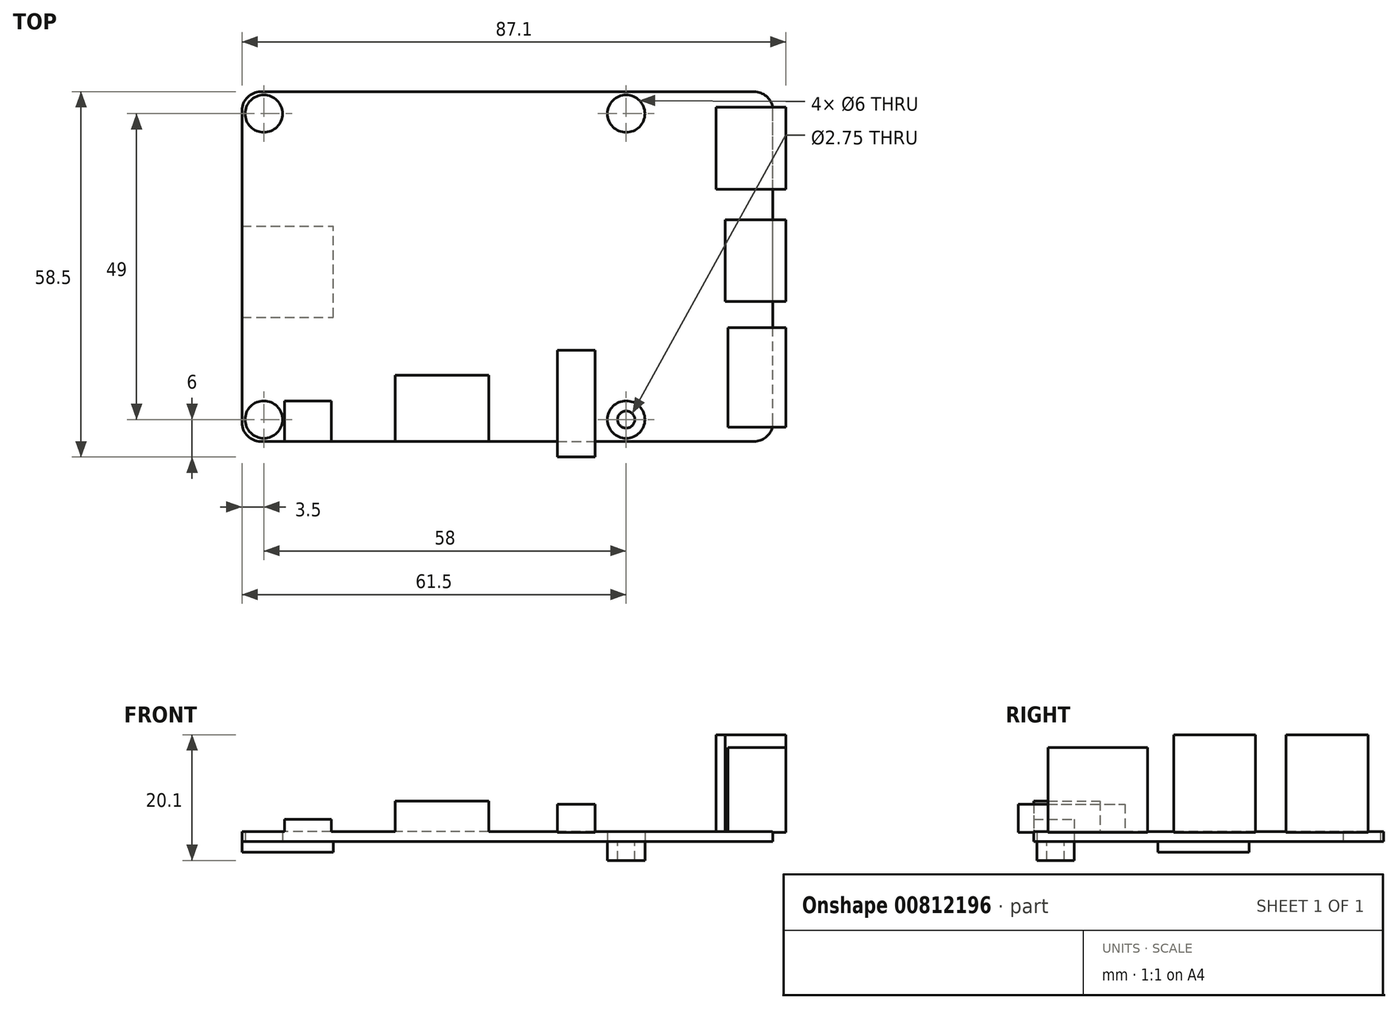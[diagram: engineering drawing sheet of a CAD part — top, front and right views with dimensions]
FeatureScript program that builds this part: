
annotation { "Feature Type Name" : "Feature", "Feature Type Description" : "" }
export const myFeature = defineFeature(function(context is Context, id is Id, definition is map)
    precondition{}
    {
        {
            var Q0;
            Q0=qCreatedBy(makeId("Top.planeOp"),FACE);
            var sketch = newSketch(context, id + "F0", { "sketchPlane" : qUnion([Q0])});
            skLineSegment(sketch, "E0.bottom", {"start": v(-39.5, -28) * mm, "end": v(39.5, -28) * mm});
            skLineSegment(sketch, "E0.top", {"start": v(-39.5, 28) * mm, "end": v(39.5, 28) * mm});
            skLineSegment(sketch, "E0.left", {"start": v(-42.5, -25) * mm, "end": v(-42.5, 25) * mm});
            skLineSegment(sketch, "E0.right", {"start": v(42.5, -25) * mm, "end": v(42.5, 25) * mm});
            skPoint(sketch, "E0.middle", {"position": v(0, 0) * mm});
            skLineSegment(sketch, "E1.bottom", {"start": v(-39, 24.5) * mm, "end": v(19, 24.5) * mm, "construction": true});
            skLineSegment(sketch, "E1.top", {"start": v(-39, -24.5) * mm, "end": v(19, -24.5) * mm, "construction": true});
            skLineSegment(sketch, "E1.left", {"start": v(-39, 24.5) * mm, "end": v(-39, -24.5) * mm, "construction": true});
            skLineSegment(sketch, "E1.right", {"start": v(19, 24.5) * mm, "end": v(19, -24.5) * mm, "construction": true});
            skCircle(sketch, "E2", {"center": v(-39, 24.5) * mm, "radius": 1.38 * mm});
            skPoint(sketch, "E3.visualSharp", {"position": v(-42.5, 28) * mm});
            skArc(sketch, "E3.filletArc", {"start": v(-39.5, 28) * mm, "mid": v(-41.62, 27.12) * mm, "end": v(-42.5, 25) * mm});
            skPoint(sketch, "E4.visualSharp", {"position": v(42.5, 28) * mm});
            skArc(sketch, "E4.filletArc", {"start": v(42.5, 25) * mm, "mid": v(41.62, 27.12) * mm, "end": v(39.5, 28) * mm});
            skPoint(sketch, "E5.visualSharp", {"position": v(-42.5, -28) * mm});
            skArc(sketch, "E5.filletArc", {"start": v(-42.5, -25) * mm, "mid": v(-41.62, -27.12) * mm, "end": v(-39.5, -28) * mm});
            skPoint(sketch, "E6.visualSharp", {"position": v(42.5, -28) * mm});
            skArc(sketch, "E6.filletArc", {"start": v(39.5, -28) * mm, "mid": v(41.62, -27.12) * mm, "end": v(42.5, -25) * mm});
            skCircle(sketch, "E7", {"center": v(19, 24.5) * mm, "radius": 1.38 * mm});
            skCircle(sketch, "E8", {"center": v(19, -24.5) * mm, "radius": 1.38 * mm});
            skCircle(sketch, "E9", {"center": v(-39, -24.5) * mm, "radius": 1.38 * mm});
            skLineSegment(sketch, "E10.bottom", {"start": v(44.6, -25.7) * mm, "end": v(35.29, -25.7) * mm});
            skLineSegment(sketch, "E10.top", {"start": v(44.6, -9.8) * mm, "end": v(35.29, -9.8) * mm});
            skLineSegment(sketch, "E10.left", {"start": v(44.6, -25.7) * mm, "end": v(44.6, -9.8) * mm});
            skLineSegment(sketch, "E10.right", {"start": v(35.29, -25.7) * mm, "end": v(35.29, -9.8) * mm});
            skLineSegment(sketch, "E11.bottom", {"start": v(44.6, -5.6) * mm, "end": v(34.86, -5.6) * mm});
            skLineSegment(sketch, "E11.top", {"start": v(44.6, 7.5) * mm, "end": v(34.86, 7.5) * mm});
            skLineSegment(sketch, "E11.left", {"start": v(44.6, -5.6) * mm, "end": v(44.6, 7.5) * mm});
            skLineSegment(sketch, "E11.right", {"start": v(34.86, -5.6) * mm, "end": v(34.86, 7.5) * mm});
            skLineSegment(sketch, "E12.bottom", {"start": v(44.6, 12.4) * mm, "end": v(33.41, 12.4) * mm});
            skLineSegment(sketch, "E12.top", {"start": v(44.6, 25.5) * mm, "end": v(33.41, 25.5) * mm});
            skLineSegment(sketch, "E12.left", {"start": v(44.6, 12.4) * mm, "end": v(44.6, 25.5) * mm});
            skLineSegment(sketch, "E12.right", {"start": v(33.41, 12.4) * mm, "end": v(33.41, 25.5) * mm});
            skLineSegment(sketch, "E13.bottom", {"start": v(-42.5, -8.1) * mm, "end": v(-27.9, -8.1) * mm});
            skLineSegment(sketch, "E13.top", {"start": v(-42.5, 6.5) * mm, "end": v(-27.9, 6.5) * mm});
            skLineSegment(sketch, "E13.left", {"start": v(-42.5, -8.1) * mm, "end": v(-42.5, 6.5) * mm});
            skLineSegment(sketch, "E13.right", {"start": v(-27.9, -8.1) * mm, "end": v(-27.9, 6.5) * mm});
            skLineSegment(sketch, "E14.bottom", {"start": v(-35.7, -28) * mm, "end": v(-28.2, -28) * mm});
            skLineSegment(sketch, "E14.top", {"start": v(-35.7, -21.5) * mm, "end": v(-28.2, -21.5) * mm});
            skLineSegment(sketch, "E14.left", {"start": v(-35.7, -28) * mm, "end": v(-35.7, -21.5) * mm});
            skLineSegment(sketch, "E14.right", {"start": v(-28.2, -28) * mm, "end": v(-28.2, -21.5) * mm});
            skLineSegment(sketch, "E15.bottom", {"start": v(-18, -28) * mm, "end": v(-3, -28) * mm});
            skLineSegment(sketch, "E15.top", {"start": v(-18, -17.42) * mm, "end": v(-3, -17.42) * mm});
            skLineSegment(sketch, "E15.left", {"start": v(-18, -28) * mm, "end": v(-18, -17.42) * mm});
            skLineSegment(sketch, "E15.right", {"start": v(-3, -28) * mm, "end": v(-3, -17.42) * mm});
            skLineSegment(sketch, "E16.bottom", {"start": v(8, -30.5) * mm, "end": v(14, -30.5) * mm});
            skLineSegment(sketch, "E16.top", {"start": v(8, -13.4) * mm, "end": v(14, -13.4) * mm});
            skLineSegment(sketch, "E16.left", {"start": v(8, -30.5) * mm, "end": v(8, -13.4) * mm});
            skLineSegment(sketch, "E16.right", {"start": v(14, -30.5) * mm, "end": v(14, -13.4) * mm});
            skCircle(sketch, "E17", {"center": v(-39, 24.5) * mm, "radius": 3 * mm});
            skCircle(sketch, "E18", {"center": v(19, 24.5) * mm, "radius": 3 * mm});
            skCircle(sketch, "E19", {"center": v(-39, -24.5) * mm, "radius": 3 * mm});
            skCircle(sketch, "E20", {"center": v(19, -24.5) * mm, "radius": 3 * mm});
            skSolve(sketch);
        }
        {
            var Q0;
            {var subQ2=sQuery(id+"F0.wireOp",EDGE,"E13.bottom");Q0=makeQuery(id+"F0.imprint","IMPRINT",FACE,{"disambiguationData":[TD([[makeQuery(id+"F0.imprint","IMPRINT",EDGE,{"derivedFrom":subQ2}),1.0]])]});}
            var Q1;
            {var subQ15=sQuery(id+"F0.wireOp",EDGE,"E0.top");Q1=makeQuery(id+"F0.imprint","IMPRINT",FACE,{"disambiguationData":[TD([[makeQuery(id+"F0.imprint","IMPRINT",EDGE,{"derivedFrom":subQ15}),-1.0]])]});}
            var Q2;
            {var subQ3=sQuery(id+"F0.wireOp",EDGE,"E10.right");Q2=makeQuery(id+"F0.imprint","IMPRINT",FACE,{"disambiguationData":[TD([[makeQuery(id+"F0.imprint","IMPRINT",EDGE,{"derivedFrom":subQ3}),-1.0]])]});}
            var Q3;
            {var subQ5=sQuery(id+"F0.wireOp",EDGE,"E11.right");Q3=makeQuery(id+"F0.imprint","IMPRINT",FACE,{"disambiguationData":[TD([[makeQuery(id+"F0.imprint","IMPRINT",EDGE,{"derivedFrom":subQ5}),-1.0]])]});}
            var Q4;
            {var subQ3=sQuery(id+"F0.wireOp",EDGE,"E12.right");Q4=makeQuery(id+"F0.imprint","IMPRINT",FACE,{"disambiguationData":[TD([[makeQuery(id+"F0.imprint","IMPRINT",EDGE,{"derivedFrom":subQ3}),-1.0]])]});}
            var Q5;
            {var subQ5=sQuery(id+"F0.wireOp",EDGE,"E16.top");Q5=makeQuery(id+"F0.imprint","IMPRINT",FACE,{"disambiguationData":[TD([[makeQuery(id+"F0.imprint","IMPRINT",EDGE,{"derivedFrom":subQ5}),-1.0]])]});}
            var Q6;
            Q6=makeQuery(id+"F0.imprint","IMPRINT",FACE,{"disambiguationData":[TD([[makeQuery(id+"F0.imprint","IMPRINT",EDGE,{"derivedFrom":sQuery(id+"F0.wireOp",EDGE,"E15.top")}),-1.0]])]});
            var Q7;
            Q7=makeQuery(id+"F0.imprint","IMPRINT",FACE,{"disambiguationData":[TD([[makeQuery(id+"F0.imprint","IMPRINT",EDGE,{"derivedFrom":sQuery(id+"F0.wireOp",EDGE,"E14.top")}),-1.0]])]});
            extrude(context, id + "F1", {"entities" : qUnion([Q0, Q1, Q2, Q3, Q4, Q5, Q6, Q7]), "depth" : 1.6 * mm, "offsetDistance" : 25 * mm});
        }
        {
            var Q0;
            {var subQ2=sQuery(id+"F0.wireOp",EDGE,"E13.bottom");Q0=makeQuery(id+"F0.imprint","IMPRINT",FACE,{"disambiguationData":[TD([[makeQuery(id+"F0.imprint","IMPRINT",EDGE,{"derivedFrom":subQ2}),1.0]])]});}
            extrude(context, id + "F2", {"entities" : qUnion([Q0]), "operationType" : NewBodyOperationType.ADD, "oppositeDirection" : true, "depth" : 1.7 * mm, "offsetDistance" : 25 * mm});
        }
        {
            var Q0;
            {var subQ5=sQuery(id+"F0.wireOp",EDGE,"E11.right");Q0=makeQuery(id+"F0.imprint","IMPRINT",FACE,{"disambiguationData":[TD([[makeQuery(id+"F0.imprint","IMPRINT",EDGE,{"derivedFrom":subQ5}),-1.0]])]});}
            var Q1;
            {var subQ5=sQuery(id+"F0.wireOp",EDGE,"E11.left");Q1=makeQuery(id+"F0.imprint","IMPRINT",FACE,{"disambiguationData":[TD([[makeQuery(id+"F0.imprint","IMPRINT",EDGE,{"derivedFrom":subQ5}),1.0]])]});}
            var Q2;
            {var subQ3=sQuery(id+"F0.wireOp",EDGE,"E12.right");Q2=makeQuery(id+"F0.imprint","IMPRINT",FACE,{"disambiguationData":[TD([[makeQuery(id+"F0.imprint","IMPRINT",EDGE,{"derivedFrom":subQ3}),-1.0]])]});}
            var Q3;
            {var subQ3=sQuery(id+"F0.wireOp",EDGE,"E12.left");Q3=makeQuery(id+"F0.imprint","IMPRINT",FACE,{"disambiguationData":[TD([[makeQuery(id+"F0.imprint","IMPRINT",EDGE,{"derivedFrom":subQ3}),1.0]])]});}
            extrude(context, id + "F3", {"entities" : qUnion([Q0, Q1, Q2, Q3]), "operationType" : NewBodyOperationType.ADD, "depth" : 17.1 * mm, "offsetDistance" : 25 * mm});
        }
        {
            var Q0;
            {var subQ3=sQuery(id+"F0.wireOp",EDGE,"E10.left");Q0=makeQuery(id+"F0.imprint","IMPRINT",FACE,{"disambiguationData":[TD([[makeQuery(id+"F0.imprint","IMPRINT",EDGE,{"derivedFrom":subQ3}),1.0]])]});}
            var Q1;
            {var subQ3=sQuery(id+"F0.wireOp",EDGE,"E10.right");Q1=makeQuery(id+"F0.imprint","IMPRINT",FACE,{"disambiguationData":[TD([[makeQuery(id+"F0.imprint","IMPRINT",EDGE,{"derivedFrom":subQ3}),-1.0]])]});}
            extrude(context, id + "F4", {"entities" : qUnion([Q0, Q1]), "operationType" : NewBodyOperationType.ADD, "depth" : 15.1 * mm, "offsetDistance" : 25 * mm});
        }
        {
            var Q0;
            {var subQ5=sQuery(id+"F0.wireOp",EDGE,"E16.top");Q0=makeQuery(id+"F0.imprint","IMPRINT",FACE,{"disambiguationData":[TD([[makeQuery(id+"F0.imprint","IMPRINT",EDGE,{"derivedFrom":subQ5}),-1.0]])]});}
            var Q1;
            {var subQ5=sQuery(id+"F0.wireOp",EDGE,"E16.bottom");Q1=makeQuery(id+"F0.imprint","IMPRINT",FACE,{"disambiguationData":[TD([[makeQuery(id+"F0.imprint","IMPRINT",EDGE,{"derivedFrom":subQ5}),1.0]])]});}
            extrude(context, id + "F5", {"entities" : qUnion([Q0, Q1]), "operationType" : NewBodyOperationType.ADD, "depth" : 6 * mm, "offsetDistance" : 25 * mm});
        }
        {
            var Q0;
            Q0=makeQuery(id+"F0.imprint","IMPRINT",FACE,{"disambiguationData":[TD([[makeQuery(id+"F0.imprint","IMPRINT",EDGE,{"derivedFrom":sQuery(id+"F0.wireOp",EDGE,"E15.top")}),-1.0]])]});
            extrude(context, id + "F6", {"entities" : qUnion([Q0]), "operationType" : NewBodyOperationType.ADD, "depth" : 6.5 * mm, "offsetDistance" : 25 * mm});
        }
        {
            var Q0;
            {var subQ3=sQuery(id+"F0.wireOp",EDGE,"E12.left");Q0=makeQuery(id+"F0.imprint","IMPRINT",FACE,{"disambiguationData":[TD([[makeQuery(id+"F0.imprint","IMPRINT",EDGE,{"derivedFrom":subQ3}),1.0]])]});}
            var Q1;
            {var subQ5=sQuery(id+"F0.wireOp",EDGE,"E11.left");Q1=makeQuery(id+"F0.imprint","IMPRINT",FACE,{"disambiguationData":[TD([[makeQuery(id+"F0.imprint","IMPRINT",EDGE,{"derivedFrom":subQ5}),1.0]])]});}
            var Q2;
            {var subQ3=sQuery(id+"F0.wireOp",EDGE,"E10.left");Q2=makeQuery(id+"F0.imprint","IMPRINT",FACE,{"disambiguationData":[TD([[makeQuery(id+"F0.imprint","IMPRINT",EDGE,{"derivedFrom":subQ3}),1.0]])]});}
            var Q3;
            {var subQ5=sQuery(id+"F0.wireOp",EDGE,"E16.bottom");Q3=makeQuery(id+"F0.imprint","IMPRINT",FACE,{"disambiguationData":[TD([[makeQuery(id+"F0.imprint","IMPRINT",EDGE,{"derivedFrom":subQ5}),1.0]])]});}
            extrude(context, id + "F7", {"entities" : qUnion([Q0, Q1, Q2, Q3]), "operationType" : NewBodyOperationType.REMOVE, "depth" : 1.5 * mm, "offsetDistance" : 25 * mm});
        }
        {
            var Q0;
            Q0=makeQuery(id+"F0.imprint","IMPRINT",FACE,{"disambiguationData":[TD([[makeQuery(id+"F0.imprint","IMPRINT",EDGE,{"derivedFrom":sQuery(id+"F0.wireOp",EDGE,"E14.top")}),-1.0]])]});
            extrude(context, id + "F8", {"entities" : qUnion([Q0]), "operationType" : NewBodyOperationType.ADD, "depth" : 3.6 * mm, "offsetDistance" : 25 * mm});
        }
        {
            var Q0;
            Q0=makeQuery(id+"F0.imprint","IMPRINT",FACE,{"disambiguationData":[TD([[makeQuery(id+"F0.imprint","IMPRINT",EDGE,{"derivedFrom":sQuery(id+"F0.wireOp",EDGE,"E8")}),-1.0]])]});
            extrude(context, id + "F9", {"entities" : qUnion([Q0]), "oppositeDirection" : true, "depth" : 3 * mm, "offsetDistance" : 25 * mm});
        }
    });
